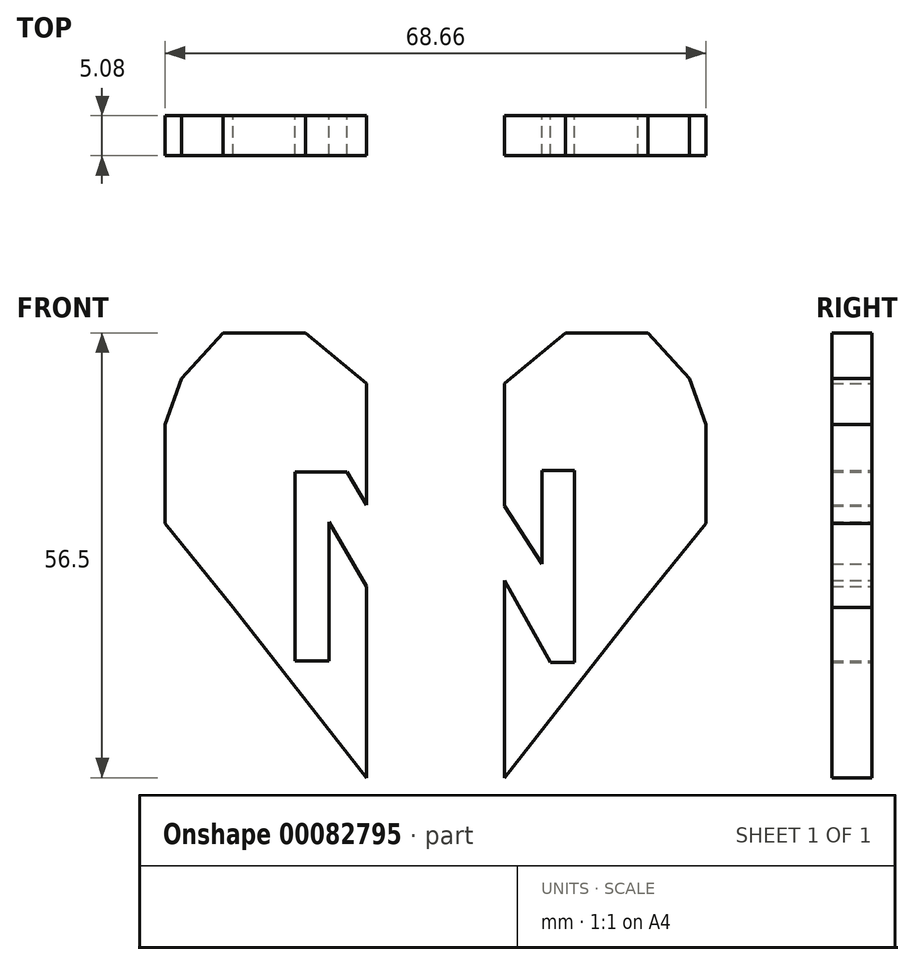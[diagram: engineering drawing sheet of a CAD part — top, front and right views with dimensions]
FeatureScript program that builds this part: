
annotation { "Feature Type Name" : "Feature", "Feature Type Description" : "" }
export const myFeature = defineFeature(function(context is Context, id is Id, definition is map)
    precondition{}
    {
        {
            var Q0;
            Q0=qCreatedBy(makeId("Front.planeOp"),FACE);
            var sketch = newSketch(context, id + "F0", { "sketchPlane" : qUnion([Q0])});
            skLineSegment(sketch, "E0", {"start": v(-8.77, 22.95) * mm, "end": v(-16.5, 29.36) * mm});
            skLineSegment(sketch, "E1", {"start": v(-16.5, 29.36) * mm, "end": v(-27.01, 29.36) * mm});
            skLineSegment(sketch, "E2", {"start": v(-27.01, 29.36) * mm, "end": v(-32.27, 23.54) * mm});
            skLineSegment(sketch, "E3", {"start": v(-32.27, 23.54) * mm, "end": v(-34.33, 17.73) * mm});
            skLineSegment(sketch, "E4", {"start": v(-34.33, 17.73) * mm, "end": v(-34.33, 5.16) * mm});
            skLineSegment(sketch, "E5", {"start": v(-34.33, 5.16) * mm, "end": v(-25.7, -5.53) * mm});
            skLineSegment(sketch, "E6", {"start": v(-25.7, -5.53) * mm, "end": v(-8.79, -27.14) * mm});
            skLineSegment(sketch, "E7", {"start": v(-8.79, -27.14) * mm, "end": v(-8.78, -2.84) * mm});
            skLineSegment(sketch, "E8.MirrorCS", {"start": v(8.77, 22.95) * mm, "end": v(16.5, 29.36) * mm});
            skLineSegment(sketch, "E9.MirrorCS", {"start": v(16.5, 29.36) * mm, "end": v(27.01, 29.36) * mm});
            skLineSegment(sketch, "E10.MirrorCS", {"start": v(34.33, 5.16) * mm, "end": v(25.7, -5.53) * mm});
            skLineSegment(sketch, "E11.MirrorCS", {"start": v(34.33, 17.73) * mm, "end": v(34.33, 5.16) * mm});
            skLineSegment(sketch, "E12.MirrorCS", {"start": v(25.7, -5.53) * mm, "end": v(8.79, -27.14) * mm});
            skLineSegment(sketch, "E13.MirrorCS", {"start": v(27.01, 29.36) * mm, "end": v(32.27, 23.54) * mm});
            skLineSegment(sketch, "E14.MirrorCS", {"start": v(8.79, -27.14) * mm, "end": v(8.78, -2.1) * mm});
            skLineSegment(sketch, "E15.MirrorCS", {"start": v(32.27, 23.54) * mm, "end": v(34.33, 17.73) * mm});
            skLineSegment(sketch, "E16", {"start": v(-8.78, 7.47) * mm, "end": v(-11.26, 11.72) * mm});
            skLineSegment(sketch, "E17", {"start": v(-11.26, 11.72) * mm, "end": v(-17.82, 11.72) * mm});
            skLineSegment(sketch, "E18", {"start": v(-17.82, 11.72) * mm, "end": v(-17.82, -12.29) * mm});
            skLineSegment(sketch, "E19", {"start": v(-17.82, -12.29) * mm, "end": v(-13.5, -12.29) * mm});
            skLineSegment(sketch, "E20", {"start": v(-13.5, -12.29) * mm, "end": v(-13.5, 5.35) * mm});
            skLineSegment(sketch, "E21", {"start": v(-13.5, 5.35) * mm, "end": v(-8.78, -2.84) * mm});
            skLineSegment(sketch, "E22.trimOffspring", {"start": v(-8.78, 7.47) * mm, "end": v(-8.77, 22.95) * mm});
            skLineSegment(sketch, "E23", {"start": v(8.78, -2.1) * mm, "end": v(14.63, -12.48) * mm});
            skLineSegment(sketch, "E24", {"start": v(14.63, -12.48) * mm, "end": v(17.63, -12.48) * mm});
            skLineSegment(sketch, "E25", {"start": v(17.63, -12.48) * mm, "end": v(17.63, 11.91) * mm});
            skLineSegment(sketch, "E26", {"start": v(17.63, 11.91) * mm, "end": v(13.5, 11.91) * mm});
            skLineSegment(sketch, "E27", {"start": v(13.5, 11.91) * mm, "end": v(13.5, 0) * mm});
            skLineSegment(sketch, "E28", {"start": v(13.5, 0) * mm, "end": v(8.78, 7.37) * mm});
            skLineSegment(sketch, "E29.trimOffspring", {"start": v(8.78, 7.37) * mm, "end": v(8.77, 22.95) * mm});
            skSolve(sketch);
        }
        {
            var Q0;
            Q0 = qSketchRegion(id + "F0", true);
            extrude(context, id + "F1", {"entities" : qUnion([Q0]), "depth" : 5.08 * mm});
        }
    });
